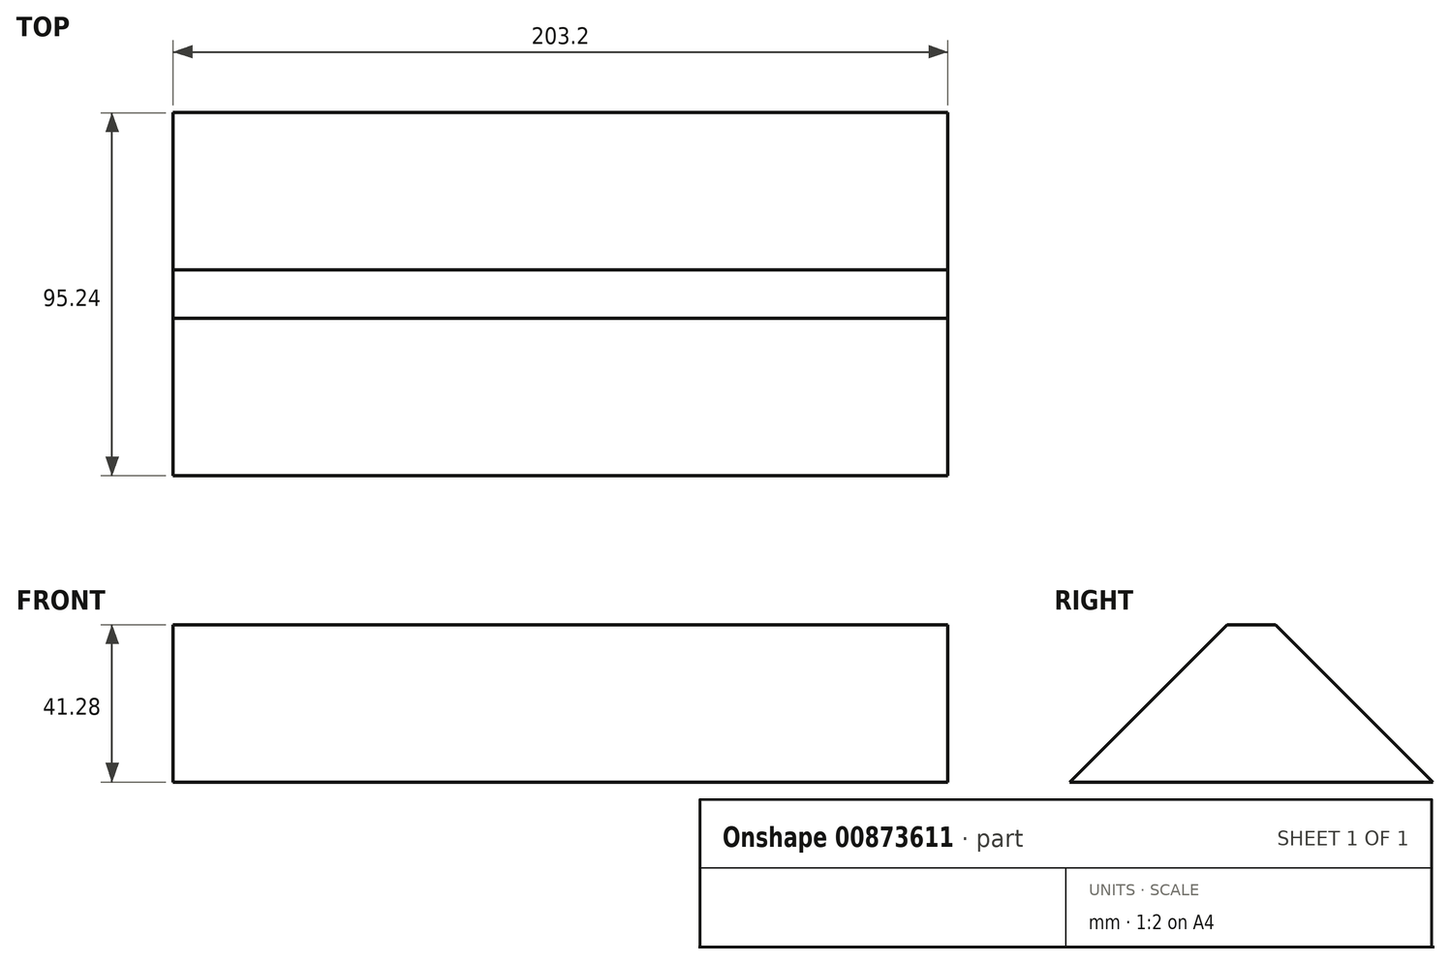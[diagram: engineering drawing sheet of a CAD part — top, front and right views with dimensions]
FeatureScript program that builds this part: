
annotation { "Feature Type Name" : "Feature", "Feature Type Description" : "" }
export const myFeature = defineFeature(function(context is Context, id is Id, definition is map)
    precondition{}
    {
        {
            var Q0;
            Q0=qCreatedBy(makeId("Right.planeOp"),FACE);
            var sketch = newSketch(context, id + "F0", { "sketchPlane" : qUnion([Q0])});
            skLineSegment(sketch, "E0.bottom", {"start": v(47.63, 20.64) * mm, "end": v(-47.63, 20.64) * mm});
            skLineSegment(sketch, "E0.top", {"start": v(47.63, -20.64) * mm, "end": v(-47.63, -20.64) * mm});
            skLineSegment(sketch, "E0.left", {"start": v(47.63, 20.64) * mm, "end": v(47.63, -20.64) * mm});
            skLineSegment(sketch, "E0.right", {"start": v(-47.63, 20.64) * mm, "end": v(-47.63, -20.64) * mm});
            skPoint(sketch, "E0.middle", {"position": v(0, 0) * mm});
            skSolve(sketch);
        }
        {
            var Q0;
            Q0=makeQuery(id+"F0.imprint","IMPRINT",FACE,{"disambiguationData":[TD([[makeQuery(id+"F0.imprint","IMPRINT",EDGE,{"derivedFrom":sQuery(id+"F0.wireOp",EDGE,"E0.bottom")}),1.0]])]});
            extrude(context, id + "F1", {"entities" : qUnion([Q0]), "oppositeDirection" : true, "depth" : 203.2 * mm, "offsetDistance" : 25.4 * mm});
        }
        {
            var Q0;
            Q0=makeQuery(id+"F1.opExtrude","SWEPT_EDGE",EDGE,{"disambiguationData":[OSD([sQuery(id+"F0.wireOp",EDGE,"E0.bottom"),sQuery(id+"F0.wireOp",EDGE,"E0.right")])]});
            var Q1;
            Q1=makeQuery(id+"F1.opExtrude","SWEPT_EDGE",EDGE,{"disambiguationData":[OSD([sQuery(id+"F0.wireOp",EDGE,"E0.bottom"),sQuery(id+"F0.wireOp",EDGE,"E0.left")])]});
            chamfer(context, id + "F2", {"entities" : qUnion([Q0, Q1]), "width" : 41.27 * mm, "tangentPropagation" : true});
        }
    });
